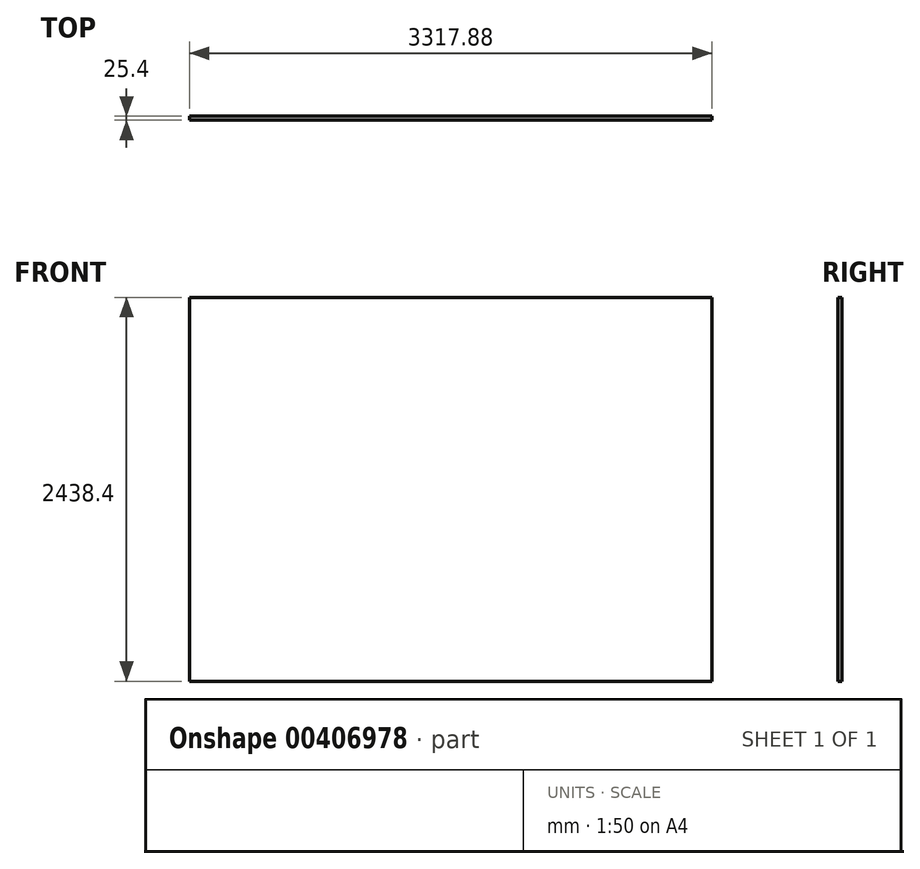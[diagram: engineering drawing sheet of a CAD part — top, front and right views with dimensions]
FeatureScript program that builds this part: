
annotation { "Feature Type Name" : "Feature", "Feature Type Description" : "" }
export const myFeature = defineFeature(function(context is Context, id is Id, definition is map)
    precondition{}
    {
        {
            var Q0;
            Q0=qCreatedBy(makeId("Top.planeOp"),FACE);
            var sketch = newSketch(context, id + "F0", { "sketchPlane" : qUnion([Q0])});
            skLineSegment(sketch, "E0.bottom", {"start": v(0, 0) * mm, "end": v(3317.88, 0) * mm, "construction": true});
            skLineSegment(sketch, "E0.top", {"start": v(0, 1754.19) * mm, "end": v(3317.88, 1754.19) * mm, "construction": true});
            skLineSegment(sketch, "E0.left", {"start": v(0, 0) * mm, "end": v(0, 1754.19) * mm, "construction": true});
            skLineSegment(sketch, "E0.right", {"start": v(3317.88, 0) * mm, "end": v(3317.88, 1754.19) * mm, "construction": true});
            skSolve(sketch);
        }
        {
            var Q0;
            Q0=qCreatedBy(makeId("Top.planeOp"),FACE);
            var sketch = newSketch(context, id + "F1", { "sketchPlane" : qUnion([Q0])});
            skCircle(sketch, "E1", {"center": v(101.6, -101.6) * mm, "radius": 25.4 * mm});
            skCircle(sketch, "E2", {"center": v(1422.4, -101.6) * mm, "radius": 25.4 * mm});
            skCircle(sketch, "E3", {"center": v(101.6, -508) * mm, "radius": 25.4 * mm});
            skCircle(sketch, "E4", {"center": v(1422.4, -508) * mm, "radius": 25.4 * mm});
            skLineSegment(sketch, "E5.bottom", {"start": v(0, 0) * mm, "end": v(1524, 0) * mm, "construction": true});
            skLineSegment(sketch, "E5.top", {"start": v(0, -609.6) * mm, "end": v(1524, -609.6) * mm, "construction": true});
            skLineSegment(sketch, "E5.left", {"start": v(0, 0) * mm, "end": v(0, -609.6) * mm, "construction": true});
            skLineSegment(sketch, "E5.right", {"start": v(1524, 0) * mm, "end": v(1524, -609.6) * mm, "construction": true});
            skLineSegment(sketch, "E6", {"start": v(101.6, -508) * mm, "end": v(1422.4, -101.6) * mm, "construction": true});
            skSolve(sketch);
        }
        {
            var Q0;
            Q0=qCreatedBy(makeId("Front.planeOp"),FACE);
            var Q1;
            Q1=sQuery(id+"F0.wireOp",VERTEX,"E0.left.end");
            cPlane(context, id + "F2", {"entities" : qUnion([Q0, Q1]), "cplaneType" : CPlaneType.PLANE_POINT, "offset" : 25.4 * mm, "width" : 152.4 * mm, "height" : 152.4 * mm});
        }
        {
            var Q0;
            Q0=qCreatedBy(id+"F2.planeOp",FACE);
            var sketch = newSketch(context, id + "F3", { "sketchPlane" : qUnion([Q0])});
            skLineSegment(sketch, "E7.bottom", {"start": v(0, 0) * mm, "end": v(3317.88, 0) * mm});
            skLineSegment(sketch, "E7.top", {"start": v(0, 2438.4) * mm, "end": v(3317.88, 2438.4) * mm});
            skLineSegment(sketch, "E7.left", {"start": v(0, 0) * mm, "end": v(0, 2438.4) * mm});
            skLineSegment(sketch, "E7.right", {"start": v(3317.88, 0) * mm, "end": v(3317.88, 2438.4) * mm});
            skSolve(sketch);
        }
        {
            var Q0;
            Q0=makeQuery(id+"F3.imprint","IMPRINT",FACE,{"disambiguationData":[TD([[makeQuery(id+"F3.imprint","IMPRINT",EDGE,{"derivedFrom":sQuery(id+"F3.wireOp",EDGE,"E7.bottom")}),1.0]])]});
            extrude(context, id + "F4", {"entities" : qUnion([Q0]), "oppositeDirection" : true, "depth" : 25.4 * mm});
        }
    });
